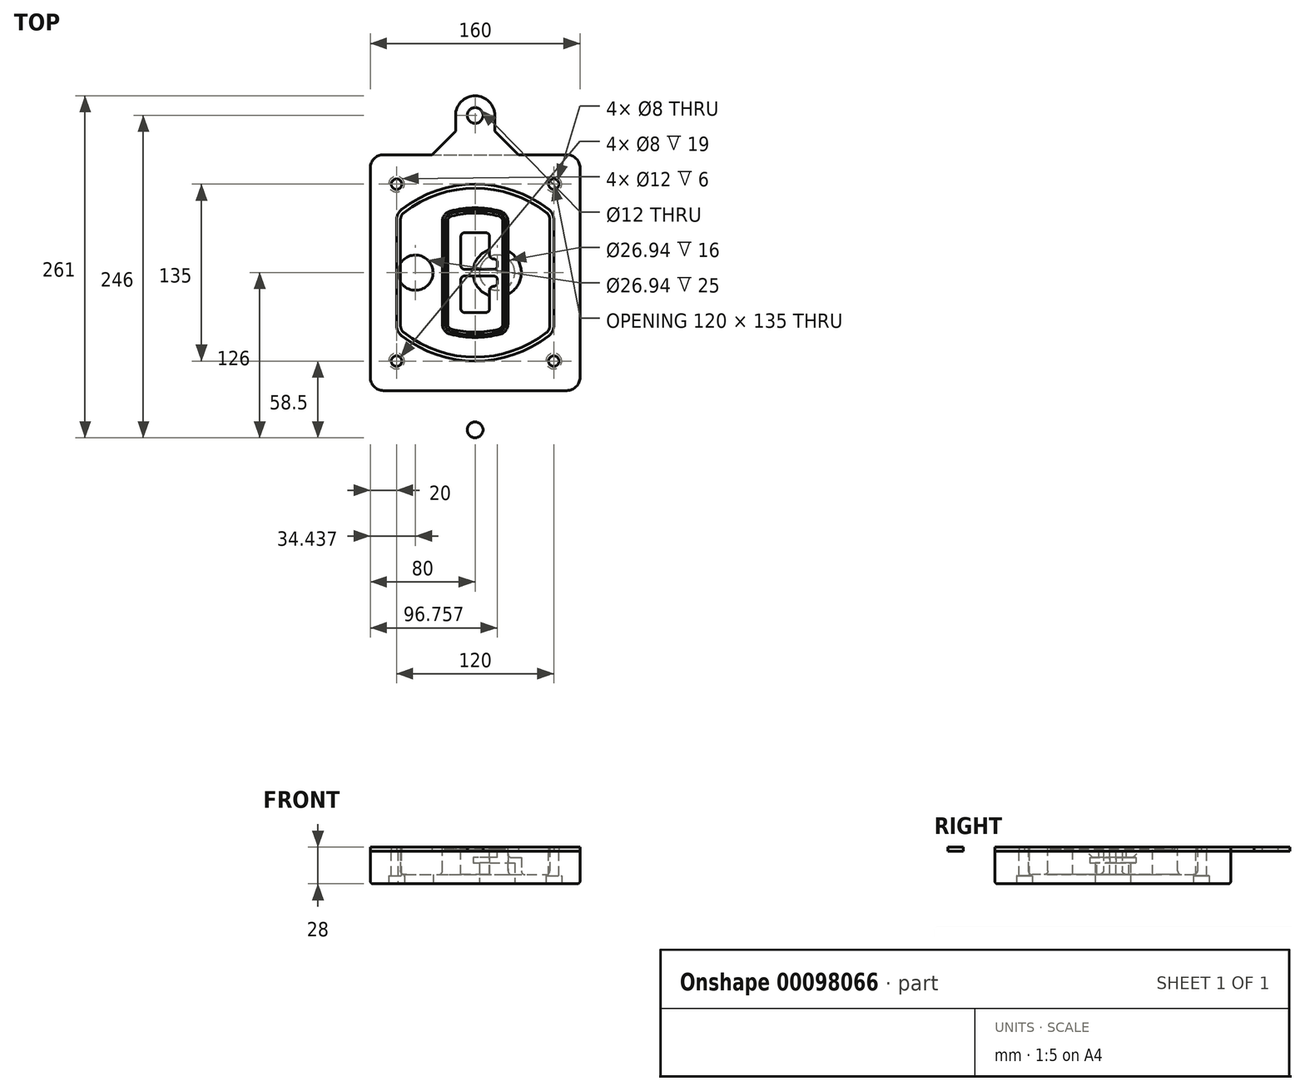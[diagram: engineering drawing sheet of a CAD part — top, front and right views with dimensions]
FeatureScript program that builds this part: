
annotation { "Feature Type Name" : "Feature", "Feature Type Description" : "" }
export const myFeature = defineFeature(function(context is Context, id is Id, definition is map)
    precondition{}
    {
        {
            var Q0;
            Q0=qCreatedBy(makeId("Top.planeOp"),FACE);
            var sketch = newSketch(context, id + "F0", { "sketchPlane" : qUnion([Q0])});
            skPoint(sketch, "E0.rect.middle", {"position": v(0, 0) * mm});
            skLineSegment(sketch, "E1.bottom", {"start": v(-70, -90) * mm, "end": v(70, -90) * mm});
            skLineSegment(sketch, "E1.top", {"start": v(-70, 90) * mm, "end": v(70, 90) * mm});
            skLineSegment(sketch, "E1.left", {"start": v(-80, -80) * mm, "end": v(-80, 80) * mm});
            skLineSegment(sketch, "E1.right", {"start": v(80, -80) * mm, "end": v(80, 80) * mm});
            skLineSegment(sketch, "E2", {"start": v(-80, 90) * mm, "end": v(80, -90) * mm, "construction": true});
            skLineSegment(sketch, "E3", {"start": v(80, 90) * mm, "end": v(-80, -90) * mm, "construction": true});
            skCircle(sketch, "E4", {"center": v(-60, 67.5) * mm, "radius": 4 * mm});
            skCircle(sketch, "E5", {"center": v(60, 67.5) * mm, "radius": 4 * mm});
            skCircle(sketch, "E6", {"center": v(60, -67.5) * mm, "radius": 4 * mm});
            skCircle(sketch, "E7", {"center": v(-60, -67.5) * mm, "radius": 4 * mm});
            skLineSegment(sketch, "E8", {"start": v(-60, 67.5) * mm, "end": v(60, 67.5) * mm, "construction": true});
            skLineSegment(sketch, "E9", {"start": v(60, 67.5) * mm, "end": v(60, -67.5) * mm, "construction": true});
            skLineSegment(sketch, "E10", {"start": v(60, -67.5) * mm, "end": v(-60, -67.5) * mm, "construction": true});
            skLineSegment(sketch, "E11", {"start": v(-60, -67.5) * mm, "end": v(-60, 67.5) * mm, "construction": true});
            skLineSegment(sketch, "E12", {"start": v(-60, 40.3) * mm, "end": v(-60, -40.3) * mm});
            skLineSegment(sketch, "E13", {"start": v(60, 40.3) * mm, "end": v(60, -40.3) * mm});
            skArc(sketch, "E14", {"start": v(56.15, 48.18) * mm, "mid": v(0, 67.5) * mm, "end": v(-56.15, 48.18) * mm});
            skArc(sketch, "E15", {"start": v(-56.15, -48.18) * mm, "mid": v(0, -67.5) * mm, "end": v(56.15, -48.18) * mm});
            skLineSegment(sketch, "E16", {"start": v(-60, 0) * mm, "end": v(60, 0) * mm, "construction": true});
            skPoint(sketch, "E17.visualSharp", {"position": v(-60, -45) * mm});
            skArc(sketch, "E17.filletArc", {"start": v(-60, -40.3) * mm, "mid": v(-58.99, -44.68) * mm, "end": v(-56.15, -48.18) * mm});
            skPoint(sketch, "E18.visualSharp", {"position": v(-60, 45) * mm});
            skArc(sketch, "E18.filletArc", {"start": v(-56.15, 48.18) * mm, "mid": v(-58.99, 44.68) * mm, "end": v(-60, 40.3) * mm});
            skPoint(sketch, "E19.visualSharp", {"position": v(60, 45) * mm});
            skArc(sketch, "E19.filletArc", {"start": v(60, 40.3) * mm, "mid": v(58.99, 44.68) * mm, "end": v(56.15, 48.18) * mm});
            skPoint(sketch, "E20.visualSharp", {"position": v(60, -45) * mm});
            skArc(sketch, "E20.filletArc", {"start": v(56.15, -48.18) * mm, "mid": v(58.99, -44.68) * mm, "end": v(60, -40.3) * mm});
            skPoint(sketch, "E21.visualSharp", {"position": v(-80, 90) * mm});
            skArc(sketch, "E21.filletArc", {"start": v(-70, 90) * mm, "mid": v(-77.07, 87.07) * mm, "end": v(-80, 80) * mm});
            skPoint(sketch, "E22.visualSharp", {"position": v(80, 90) * mm});
            skArc(sketch, "E22.filletArc", {"start": v(80, 80) * mm, "mid": v(77.07, 87.07) * mm, "end": v(70, 90) * mm});
            skPoint(sketch, "E23.visualSharp", {"position": v(80, -90) * mm});
            skArc(sketch, "E23.filletArc", {"start": v(70, -90) * mm, "mid": v(77.07, -87.07) * mm, "end": v(80, -80) * mm});
            skPoint(sketch, "E24.visualSharp", {"position": v(-80, -90) * mm});
            skArc(sketch, "E24.filletArc", {"start": v(-80, -80) * mm, "mid": v(-77.07, -87.07) * mm, "end": v(-70, -90) * mm});
            skArc(sketch, "E25.0", {"start": v(57, 40.3) * mm, "mid": v(56.3, 43.36) * mm, "end": v(54.3, 45.81) * mm});
            skLineSegment(sketch, "E25.1", {"start": v(57, 40.3) * mm, "end": v(57, -40.3) * mm});
            skArc(sketch, "E25.2", {"start": v(54.3, -45.81) * mm, "mid": v(56.3, -43.36) * mm, "end": v(57, -40.3) * mm});
            skArc(sketch, "E25.3", {"start": v(-54.3, -45.81) * mm, "mid": v(0, -64.5) * mm, "end": v(54.3, -45.81) * mm});
            skArc(sketch, "E25.4", {"start": v(-57, -40.3) * mm, "mid": v(-56.3, -43.36) * mm, "end": v(-54.3, -45.81) * mm});
            skArc(sketch, "E25.5", {"start": v(54.3, 45.81) * mm, "mid": v(0, 64.5) * mm, "end": v(-54.3, 45.81) * mm});
            skLineSegment(sketch, "E25.6", {"start": v(-57, 40.3) * mm, "end": v(-57, -40.3) * mm});
            skArc(sketch, "E25.7", {"start": v(-54.3, 45.81) * mm, "mid": v(-56.3, 43.36) * mm, "end": v(-57, 40.3) * mm});
            skArc(sketch, "E26.0", {"start": v(-58.62, 51.33) * mm, "mid": v(-62.58, 46.43) * mm, "end": v(-64, 40.3) * mm});
            skArc(sketch, "E26.1", {"start": v(58.62, 51.33) * mm, "mid": v(0, 71.5) * mm, "end": v(-58.62, 51.33) * mm});
            skArc(sketch, "E26.2", {"start": v(64, 40.3) * mm, "mid": v(62.58, 46.43) * mm, "end": v(58.62, 51.33) * mm});
            skLineSegment(sketch, "E26.3", {"start": v(64, 40.3) * mm, "end": v(64, -40.3) * mm});
            skArc(sketch, "E26.4", {"start": v(58.62, -51.33) * mm, "mid": v(62.58, -46.43) * mm, "end": v(64, -40.3) * mm});
            skLineSegment(sketch, "E26.5", {"start": v(-64, 40.3) * mm, "end": v(-64, -40.3) * mm});
            skArc(sketch, "E26.6", {"start": v(-58.62, -51.33) * mm, "mid": v(0, -71.5) * mm, "end": v(58.62, -51.33) * mm});
            skArc(sketch, "E26.7", {"start": v(-64, -40.3) * mm, "mid": v(-62.58, -46.43) * mm, "end": v(-58.62, -51.33) * mm});
            skSolve(sketch);
        }
        {
            var Q0;
            Q0=makeQuery(id+"F0.imprint","IMPRINT",FACE,{"disambiguationData":[TD([[makeQuery(id+"F0.imprint","IMPRINT",EDGE,{"derivedFrom":sQuery(id+"F0.wireOp",EDGE,"E1.bottom")}),1.0]])]});
            var Q1;
            Q1=makeQuery(id+"F0.imprint","IMPRINT",FACE,{"disambiguationData":[TD([[makeQuery(id+"F0.imprint","IMPRINT",EDGE,{"derivedFrom":sQuery(id+"F0.wireOp",EDGE,"E12")}),1.0]])]});
            var Q2;
            Q2=makeQuery(id+"F0.imprint","IMPRINT",FACE,{"disambiguationData":[TD([[makeQuery(id+"F0.imprint","IMPRINT",EDGE,{"derivedFrom":sQuery(id+"F0.wireOp",EDGE,"E25.0")}),1.0]])]});
            var Q3;
            Q3=makeQuery(id+"F0.imprint","IMPRINT",FACE,{"disambiguationData":[TD([[makeQuery(id+"F0.imprint","IMPRINT",EDGE,{"derivedFrom":sQuery(id+"F0.wireOp",EDGE,"E12")}),-1.0]])]});
            extrude(context, id + "F1", {"entities" : qUnion([Q0, Q1, Q2, Q3]), "oppositeDirection" : true, "depth" : 25 * mm});
        }
        {
            var Q0;
            Q0=makeQuery(id+"F0.imprint","IMPRINT",FACE,{"disambiguationData":[TD([[makeQuery(id+"F0.imprint","IMPRINT",EDGE,{"derivedFrom":sQuery(id+"F0.wireOp",EDGE,"E12")}),1.0]])]});
            extrude(context, id + "F2", {"entities" : qUnion([Q0]), "operationType" : NewBodyOperationType.ADD, "depth" : 3 * mm});
        }
        {
            var Q0;
            Q0=makeQuery(id+"F0.imprint","IMPRINT",FACE,{"disambiguationData":[TD([[makeQuery(id+"F0.imprint","IMPRINT",EDGE,{"derivedFrom":sQuery(id+"F0.wireOp",EDGE,"E25.0")}),1.0]])]});
            extrude(context, id + "F3", {"entities" : qUnion([Q0]), "operationType" : NewBodyOperationType.REMOVE, "oppositeDirection" : true, "depth" : 18 * mm});
        }
        {
            var Q0;
            Q0=makeQuery(id+"F2.opExtrude","CAP_FACE",FACE,{"disambiguationData":[OSD([sQuery(id+"F0.wireOp",EDGE,"E12"),sQuery(id+"F0.wireOp",EDGE,"E13"),sQuery(id+"F0.wireOp",EDGE,"E14"),sQuery(id+"F0.wireOp",EDGE,"E15"),sQuery(id+"F0.wireOp",EDGE,"E17.filletArc"),sQuery(id+"F0.wireOp",EDGE,"E18.filletArc"),sQuery(id+"F0.wireOp",EDGE,"E19.filletArc"),sQuery(id+"F0.wireOp",EDGE,"E20.filletArc"),sQuery(id+"F0.wireOp",EDGE,"E25.0"),sQuery(id+"F0.wireOp",EDGE,"E25.1"),sQuery(id+"F0.wireOp",EDGE,"E25.2"),sQuery(id+"F0.wireOp",EDGE,"E25.3"),sQuery(id+"F0.wireOp",EDGE,"E25.4"),sQuery(id+"F0.wireOp",EDGE,"E25.5"),sQuery(id+"F0.wireOp",EDGE,"E25.6"),sQuery(id+"F0.wireOp",EDGE,"E25.7")])],"isStart":false});
            var sketch = newSketch(context, id + "F4", { "sketchPlane" : qUnion([Q0])});
            skArc(sketch, "E27.0", {"start": v(-19.08, -46.97) * mm, "mid": v(0, -49.5) * mm, "end": v(19.08, -46.97) * mm});
            skArc(sketch, "E28.0", {"start": v(19.08, 46.97) * mm, "mid": v(0, 49.5) * mm, "end": v(-19.08, 46.97) * mm});
            skLineSegment(sketch, "E29", {"start": v(-25, 39.25) * mm, "end": v(-25, -39.25) * mm});
            skLineSegment(sketch, "E30", {"start": v(25, 39.25) * mm, "end": v(25, -39.25) * mm});
            skLineSegment(sketch, "E31", {"start": v(-25, 45.1) * mm, "end": v(25, 45.1) * mm, "construction": true});
            skLineSegment(sketch, "E32", {"start": v(-25, -45.1) * mm, "end": v(25, -45.1) * mm, "construction": true});
            skPoint(sketch, "E33.visualSharp", {"position": v(-25, 45.1) * mm});
            skArc(sketch, "E33.filletArc", {"start": v(-19.08, 46.97) * mm, "mid": v(-23.35, 44.11) * mm, "end": v(-25, 39.25) * mm});
            skPoint(sketch, "E34.visualSharp", {"position": v(25, 45.1) * mm});
            skArc(sketch, "E34.filletArc", {"start": v(25, 39.25) * mm, "mid": v(23.35, 44.11) * mm, "end": v(19.08, 46.97) * mm});
            skPoint(sketch, "E35.visualSharp", {"position": v(25, -45.1) * mm});
            skArc(sketch, "E35.filletArc", {"start": v(19.08, -46.97) * mm, "mid": v(23.35, -44.11) * mm, "end": v(25, -39.25) * mm});
            skPoint(sketch, "E36.visualSharp", {"position": v(-25, -45.1) * mm});
            skArc(sketch, "E36.filletArc", {"start": v(-25, -39.25) * mm, "mid": v(-23.35, -44.11) * mm, "end": v(-19.08, -46.97) * mm});
            skArc(sketch, "E37.0", {"start": v(54.3, 45.81) * mm, "mid": v(0, 64.5) * mm, "end": v(-54.3, 45.81) * mm});
            skArc(sketch, "E37.1", {"start": v(-54.3, 45.81) * mm, "mid": v(-56.3, 43.36) * mm, "end": v(-57, 40.3) * mm});
            skLineSegment(sketch, "E37.2", {"start": v(-57, 40.3) * mm, "end": v(-57, -40.3) * mm});
            skArc(sketch, "E37.3", {"start": v(-57, -40.3) * mm, "mid": v(-56.3, -43.36) * mm, "end": v(-54.3, -45.81) * mm});
            skArc(sketch, "E37.4", {"start": v(-54.3, -45.81) * mm, "mid": v(0, -64.5) * mm, "end": v(54.3, -45.81) * mm});
            skArc(sketch, "E37.5", {"start": v(54.3, -45.81) * mm, "mid": v(56.3, -43.36) * mm, "end": v(57, -40.3) * mm});
            skLineSegment(sketch, "E37.6", {"start": v(57, 40.3) * mm, "end": v(57, -40.3) * mm});
            skArc(sketch, "E37.7", {"start": v(57, 40.3) * mm, "mid": v(56.3, 43.36) * mm, "end": v(54.3, 45.81) * mm});
            skLineSegment(sketch, "E38.0", {"start": v(23, 39.25) * mm, "end": v(23, -39.25) * mm});
            skArc(sketch, "E38.1", {"start": v(18.56, -45.04) * mm, "mid": v(21.76, -42.9) * mm, "end": v(23, -39.25) * mm});
            skArc(sketch, "E38.2", {"start": v(-18.56, -45.04) * mm, "mid": v(0, -47.5) * mm, "end": v(18.56, -45.04) * mm});
            skArc(sketch, "E38.3", {"start": v(-23, -39.25) * mm, "mid": v(-21.76, -42.9) * mm, "end": v(-18.56, -45.04) * mm});
            skLineSegment(sketch, "E38.4", {"start": v(-23, 39.25) * mm, "end": v(-23, -39.25) * mm});
            skArc(sketch, "E38.5", {"start": v(23, 39.25) * mm, "mid": v(21.76, 42.9) * mm, "end": v(18.56, 45.04) * mm});
            skArc(sketch, "E38.6", {"start": v(-18.56, 45.04) * mm, "mid": v(-21.76, 42.9) * mm, "end": v(-23, 39.25) * mm});
            skArc(sketch, "E38.7", {"start": v(18.56, 45.04) * mm, "mid": v(0, 47.5) * mm, "end": v(-18.56, 45.04) * mm});
            skArc(sketch, "E39.0", {"start": v(21, 39.25) * mm, "mid": v(20.18, 41.68) * mm, "end": v(18.04, 43.1) * mm});
            skLineSegment(sketch, "E39.1", {"start": v(21, 39.25) * mm, "end": v(21, -39.25) * mm});
            skArc(sketch, "E39.2", {"start": v(18.04, -43.1) * mm, "mid": v(20.18, -41.68) * mm, "end": v(21, -39.25) * mm});
            skArc(sketch, "E39.3", {"start": v(-18.04, -43.1) * mm, "mid": v(0, -45.5) * mm, "end": v(18.04, -43.1) * mm});
            skArc(sketch, "E39.4", {"start": v(-21, -39.25) * mm, "mid": v(-20.18, -41.68) * mm, "end": v(-18.04, -43.1) * mm});
            skArc(sketch, "E39.5", {"start": v(18.04, 43.1) * mm, "mid": v(0, 45.5) * mm, "end": v(-18.04, 43.1) * mm});
            skLineSegment(sketch, "E39.6", {"start": v(-21, 39.25) * mm, "end": v(-21, -39.25) * mm});
            skArc(sketch, "E39.7", {"start": v(-18.04, 43.1) * mm, "mid": v(-20.18, 41.68) * mm, "end": v(-21, 39.25) * mm});
            skLineSegment(sketch, "E40", {"start": v(-25, 0) * mm, "end": v(25, 0) * mm, "construction": true});
            skLineSegment(sketch, "E41", {"start": v(-11, 5.5) * mm, "end": v(-11, 27.5) * mm});
            skLineSegment(sketch, "E42", {"start": v(-8, 30.5) * mm, "end": v(8, 30.5) * mm});
            skLineSegment(sketch, "E43", {"start": v(11, 27.5) * mm, "end": v(11, 13.5) * mm});
            skLineSegment(sketch, "E44", {"start": v(14, 10.5) * mm, "end": v(14, 10.5) * mm});
            skLineSegment(sketch, "E45", {"start": v(17, 7.5) * mm, "end": v(17, 5.5) * mm});
            skLineSegment(sketch, "E46", {"start": v(14, 2.5) * mm, "end": v(-8, 2.5) * mm});
            skPoint(sketch, "E47.visualSharp", {"position": v(-11, 30.5) * mm});
            skArc(sketch, "E47.filletArc", {"start": v(-8, 30.5) * mm, "mid": v(-10.12, 29.62) * mm, "end": v(-11, 27.5) * mm});
            skPoint(sketch, "E48.visualSharp", {"position": v(11, 30.5) * mm});
            skArc(sketch, "E48.filletArc", {"start": v(11, 27.5) * mm, "mid": v(10.12, 29.62) * mm, "end": v(8, 30.5) * mm});
            skPoint(sketch, "E49.visualSharp", {"position": v(11, 10.5) * mm});
            skArc(sketch, "E49.filletArc", {"start": v(11, 13.5) * mm, "mid": v(11.88, 11.38) * mm, "end": v(14, 10.5) * mm});
            skPoint(sketch, "E50.visualSharp", {"position": v(17, 10.5) * mm});
            skArc(sketch, "E50.filletArc", {"start": v(17, 7.5) * mm, "mid": v(16.12, 9.62) * mm, "end": v(14, 10.5) * mm});
            skPoint(sketch, "E51.visualSharp", {"position": v(17, 2.5) * mm});
            skArc(sketch, "E51.filletArc", {"start": v(14, 2.5) * mm, "mid": v(16.12, 3.38) * mm, "end": v(17, 5.5) * mm});
            skPoint(sketch, "E52.visualSharp", {"position": v(-11, 2.5) * mm});
            skArc(sketch, "E52.filletArc", {"start": v(-11, 5.5) * mm, "mid": v(-10.12, 3.38) * mm, "end": v(-8, 2.5) * mm});
            skLineSegment(sketch, "E53.0.MirrorCS", {"start": v(14, -2.5) * mm, "end": v(-8, -2.5) * mm});
            skArc(sketch, "E54.0.MirrorCS", {"start": v(-11, -5.5) * mm, "mid": v(-10.12, -3.38) * mm, "end": v(-8, -2.5) * mm});
            skLineSegment(sketch, "E55.0.MirrorCS", {"start": v(-11, -5.5) * mm, "end": v(-11, -27.5) * mm});
            skArc(sketch, "E56.0.MirrorCS", {"start": v(-8, -30.5) * mm, "mid": v(-10.12, -29.62) * mm, "end": v(-11, -27.5) * mm});
            skLineSegment(sketch, "E57.0.MirrorCS", {"start": v(-8, -30.5) * mm, "end": v(8, -30.5) * mm});
            skArc(sketch, "E58.0.MirrorCS", {"start": v(11, -27.5) * mm, "mid": v(10.12, -29.62) * mm, "end": v(8, -30.5) * mm});
            skLineSegment(sketch, "E59.0.MirrorCS", {"start": v(11, -27.5) * mm, "end": v(11, -13.5) * mm});
            skArc(sketch, "E60.0.MirrorCS", {"start": v(11, -13.5) * mm, "mid": v(11.88, -11.38) * mm, "end": v(14, -10.5) * mm});
            skArc(sketch, "E61.0.MirrorCS", {"start": v(17, -7.5) * mm, "mid": v(16.12, -9.62) * mm, "end": v(14, -10.5) * mm});
            skLineSegment(sketch, "E62.0.MirrorCS", {"start": v(17, -7.5) * mm, "end": v(17, -5.5) * mm});
            skArc(sketch, "E63.0.MirrorCS", {"start": v(14, -2.5) * mm, "mid": v(16.12, -3.38) * mm, "end": v(17, -5.5) * mm});
            skSolve(sketch);
        }
        {
            var Q0;
            Q0=makeQuery(id+"F4.imprint","IMPRINT",FACE,{"disambiguationData":[TD([[makeQuery(id+"F4.imprint","IMPRINT",EDGE,{"derivedFrom":sQuery(id+"F4.wireOp",EDGE,"E27.0")}),1.0]])]});
            var Q1;
            Q1=makeQuery(id+"F4.imprint","IMPRINT",FACE,{"disambiguationData":[TD([[makeQuery(id+"F4.imprint","IMPRINT",EDGE,{"derivedFrom":sQuery(id+"F4.wireOp",EDGE,"E38.0")}),-1.0]])]});
            var Q2;
            Q2=makeQuery(id+"F4.imprint","IMPRINT",FACE,{"disambiguationData":[TD([[makeQuery(id+"F4.imprint","IMPRINT",EDGE,{"derivedFrom":sQuery(id+"F4.wireOp",EDGE,"E39.0")}),1.0]])]});
            extrude(context, id + "F5", {"entities" : qUnion([Q0, Q1, Q2]), "operationType" : NewBodyOperationType.ADD, "endBound" : BoundingType.UP_TO_NEXT, "oppositeDirection" : true, "depth" : 25 * mm});
        }
        {
            var Q0;
            Q0=makeQuery(id+"F4.imprint","IMPRINT",FACE,{"disambiguationData":[TD([[makeQuery(id+"F4.imprint","IMPRINT",EDGE,{"derivedFrom":sQuery(id+"F4.wireOp",EDGE,"E38.0")}),-1.0]])]});
            extrude(context, id + "F6", {"entities" : qUnion([Q0]), "operationType" : NewBodyOperationType.REMOVE, "oppositeDirection" : true, "depth" : 2 * mm});
        }
        {
            var Q0;
            Q0=makeQuery(id+"F1.opExtrude","CAP_FACE",FACE,{"disambiguationData":[OSD([sQuery(id+"F0.wireOp",EDGE,"E1.bottom"),sQuery(id+"F0.wireOp",EDGE,"E1.top"),sQuery(id+"F0.wireOp",EDGE,"E1.left"),sQuery(id+"F0.wireOp",EDGE,"E1.right"),sQuery(id+"F0.wireOp",EDGE,"E4"),sQuery(id+"F0.wireOp",EDGE,"E5"),sQuery(id+"F0.wireOp",EDGE,"E6"),sQuery(id+"F0.wireOp",EDGE,"E7"),sQuery(id+"F0.wireOp",EDGE,"E21.filletArc"),sQuery(id+"F0.wireOp",EDGE,"E22.filletArc"),sQuery(id+"F0.wireOp",EDGE,"E23.filletArc"),sQuery(id+"F0.wireOp",EDGE,"E24.filletArc")])],"isStart":false});
            var sketch = newSketch(context, id + "F7", { "sketchPlane" : qUnion([Q0])});
            skCircle(sketch, "E64", {"center": v(16.76, 0) * mm, "radius": 13.47 * mm});
            skCircle(sketch, "E65", {"center": v(-45.56, 0) * mm, "radius": 13.47 * mm});
            skLineSegment(sketch, "E66", {"start": v(80, 0) * mm, "end": v(-80, 0) * mm});
            skCircle(sketch, "E67", {"center": v(16.76, 0) * mm, "radius": 18.47 * mm});
            skCircle(sketch, "E68", {"center": v(60, -67.5) * mm, "radius": 6 * mm});
            skCircle(sketch, "E69", {"center": v(-60, -67.5) * mm, "radius": 6 * mm});
            skCircle(sketch, "E70", {"center": v(-60, 67.5) * mm, "radius": 6 * mm});
            skCircle(sketch, "E71", {"center": v(60, 67.5) * mm, "radius": 6 * mm});
            skSolve(sketch);
        }
        {
            var Q0;
            {var subQ1=sQuery(id+"F7.wireOp",EDGE,"E66");var subQ4=sQuery(id+"F7.wireOp",EDGE,"E64");var subQ6=makeQuery(id+"F7.imprint","INTERSECT",VERTEX,{"disambiguationData":[OD(0.0)],"derivedFrom":[subQ4,subQ1]});Q0=makeQuery(id+"F7.imprint","IMPRINT",FACE,{"disambiguationData":[TD([[makeQuery(id+"F7.imprint","IMPRINT",EDGE,{"disambiguationData":[TD([[subQ6,-1.0]])],"derivedFrom":subQ4}),-1.0]])]});}
            var Q1;
            {var subQ0=sQuery(id+"F7.wireOp",EDGE,"E66");var subQ1=sQuery(id+"F7.wireOp",EDGE,"E64");var subQ3=makeQuery(id+"F7.imprint","INTERSECT",VERTEX,{"disambiguationData":[OD(0.0)],"derivedFrom":[subQ1,subQ0]});Q1=makeQuery(id+"F7.imprint","IMPRINT",FACE,{"disambiguationData":[TD([[makeQuery(id+"F7.imprint","IMPRINT",EDGE,{"disambiguationData":[TD([[subQ3,-1.0]])],"derivedFrom":subQ1}),1.0]])]});}
            var Q2;
            {var subQ0=sQuery(id+"F7.wireOp",EDGE,"E66");var subQ1=sQuery(id+"F7.wireOp",EDGE,"E64");var subQ3=makeQuery(id+"F7.imprint","INTERSECT",VERTEX,{"disambiguationData":[OD(0.0)],"derivedFrom":[subQ1,subQ0]});Q2=makeQuery(id+"F7.imprint","IMPRINT",FACE,{"disambiguationData":[TD([[makeQuery(id+"F7.imprint","IMPRINT",EDGE,{"disambiguationData":[TD([[subQ3,1.0]])],"derivedFrom":subQ1}),1.0]])]});}
            var Q3;
            {var subQ1=sQuery(id+"F7.wireOp",EDGE,"E66");var subQ4=sQuery(id+"F7.wireOp",EDGE,"E64");var subQ6=makeQuery(id+"F7.imprint","INTERSECT",VERTEX,{"disambiguationData":[OD(0.0)],"derivedFrom":[subQ4,subQ1]});Q3=makeQuery(id+"F7.imprint","IMPRINT",FACE,{"disambiguationData":[TD([[makeQuery(id+"F7.imprint","IMPRINT",EDGE,{"disambiguationData":[TD([[subQ6,1.0]])],"derivedFrom":subQ4}),-1.0]])]});}
            extrude(context, id + "F8", {"entities" : qUnion([Q0, Q1, Q2, Q3]), "operationType" : NewBodyOperationType.ADD, "oppositeDirection" : true, "depth" : 20 * mm});
        }
        {
            var Q0;
            {var subQ0=sQuery(id+"F7.wireOp",EDGE,"E66");var subQ1=sQuery(id+"F7.wireOp",EDGE,"E64");var subQ3=makeQuery(id+"F7.imprint","INTERSECT",VERTEX,{"disambiguationData":[OD(0.0)],"derivedFrom":[subQ1,subQ0]});Q0=makeQuery(id+"F7.imprint","IMPRINT",FACE,{"disambiguationData":[TD([[makeQuery(id+"F7.imprint","IMPRINT",EDGE,{"disambiguationData":[TD([[subQ3,-1.0]])],"derivedFrom":subQ1}),1.0]])]});}
            var Q1;
            {var subQ0=sQuery(id+"F7.wireOp",EDGE,"E66");var subQ1=sQuery(id+"F7.wireOp",EDGE,"E64");var subQ3=makeQuery(id+"F7.imprint","INTERSECT",VERTEX,{"disambiguationData":[OD(0.0)],"derivedFrom":[subQ1,subQ0]});Q1=makeQuery(id+"F7.imprint","IMPRINT",FACE,{"disambiguationData":[TD([[makeQuery(id+"F7.imprint","IMPRINT",EDGE,{"disambiguationData":[TD([[subQ3,1.0]])],"derivedFrom":subQ1}),1.0]])]});}
            extrude(context, id + "F9", {"entities" : qUnion([Q0, Q1]), "operationType" : NewBodyOperationType.REMOVE, "oppositeDirection" : true, "depth" : 16 * mm});
        }
        {
            var Q0;
            {var subQ0=sQuery(id+"F7.wireOp",EDGE,"E66");var subQ1=sQuery(id+"F7.wireOp",EDGE,"E65");var subQ3=makeQuery(id+"F7.imprint","INTERSECT",VERTEX,{"disambiguationData":[OD(0.0)],"derivedFrom":[subQ1,subQ0]});Q0=makeQuery(id+"F7.imprint","IMPRINT",FACE,{"disambiguationData":[TD([[makeQuery(id+"F7.imprint","IMPRINT",EDGE,{"disambiguationData":[TD([[subQ3,-1.0]])],"derivedFrom":subQ1}),1.0]])]});}
            var Q1;
            {var subQ0=sQuery(id+"F7.wireOp",EDGE,"E66");var subQ1=sQuery(id+"F7.wireOp",EDGE,"E65");var subQ3=makeQuery(id+"F7.imprint","INTERSECT",VERTEX,{"disambiguationData":[OD(0.0)],"derivedFrom":[subQ1,subQ0]});Q1=makeQuery(id+"F7.imprint","IMPRINT",FACE,{"disambiguationData":[TD([[makeQuery(id+"F7.imprint","IMPRINT",EDGE,{"disambiguationData":[TD([[subQ3,1.0]])],"derivedFrom":subQ1}),1.0]])]});}
            extrude(context, id + "F10", {"entities" : qUnion([Q0, Q1]), "operationType" : NewBodyOperationType.REMOVE, "oppositeDirection" : true, "depth" : 25 * mm});
        }
        {
            var Q0;
            Q0=makeQuery(id+"F7.imprint","IMPRINT",FACE,{"disambiguationData":[TD([[makeQuery(id+"F7.imprint","IMPRINT",EDGE,{"derivedFrom":sQuery(id+"F7.wireOp",EDGE,"E68")}),1.0]])]});
            var Q1;
            Q1=makeQuery(id+"F7.imprint","IMPRINT",FACE,{"disambiguationData":[TD([[makeQuery(id+"F7.imprint","IMPRINT",EDGE,{"derivedFrom":makeQuery(id+"F1.opExtrude","CAP_EDGE",EDGE,{"disambiguationData":[OSD([sQuery(id+"F0.wireOp",EDGE,"E5")])],"isStart":false})}),-1.0]])]});
            var Q2;
            Q2=makeQuery(id+"F7.imprint","IMPRINT",FACE,{"disambiguationData":[TD([[makeQuery(id+"F7.imprint","IMPRINT",EDGE,{"derivedFrom":sQuery(id+"F7.wireOp",EDGE,"E69")}),1.0]])]});
            var Q3;
            Q3=makeQuery(id+"F7.imprint","IMPRINT",FACE,{"disambiguationData":[TD([[makeQuery(id+"F7.imprint","IMPRINT",EDGE,{"derivedFrom":makeQuery(id+"F1.opExtrude","CAP_EDGE",EDGE,{"disambiguationData":[OSD([sQuery(id+"F0.wireOp",EDGE,"E4")])],"isStart":false})}),-1.0]])]});
            var Q4;
            Q4=makeQuery(id+"F7.imprint","IMPRINT",FACE,{"disambiguationData":[TD([[makeQuery(id+"F7.imprint","IMPRINT",EDGE,{"derivedFrom":sQuery(id+"F7.wireOp",EDGE,"E70")}),1.0]])]});
            var Q5;
            Q5=makeQuery(id+"F7.imprint","IMPRINT",FACE,{"disambiguationData":[TD([[makeQuery(id+"F7.imprint","IMPRINT",EDGE,{"derivedFrom":makeQuery(id+"F1.opExtrude","CAP_EDGE",EDGE,{"disambiguationData":[OSD([sQuery(id+"F0.wireOp",EDGE,"E7")])],"isStart":false})}),-1.0]])]});
            var Q6;
            Q6=makeQuery(id+"F7.imprint","IMPRINT",FACE,{"disambiguationData":[TD([[makeQuery(id+"F7.imprint","IMPRINT",EDGE,{"derivedFrom":sQuery(id+"F7.wireOp",EDGE,"E71")}),1.0]])]});
            var Q7;
            Q7=makeQuery(id+"F7.imprint","IMPRINT",FACE,{"disambiguationData":[TD([[makeQuery(id+"F7.imprint","IMPRINT",EDGE,{"derivedFrom":makeQuery(id+"F1.opExtrude","CAP_EDGE",EDGE,{"disambiguationData":[OSD([sQuery(id+"F0.wireOp",EDGE,"E6")])],"isStart":false})}),-1.0]])]});
            extrude(context, id + "F11", {"entities" : qUnion([Q0, Q1, Q2, Q3, Q4, Q5, Q6, Q7]), "operationType" : NewBodyOperationType.REMOVE, "oppositeDirection" : true, "depth" : 6 * mm});
        }
        {
            var Q0;
            Q0=makeQuery(id+"F9.boolean.opBoolean","COPY",FACE,{"derivedFrom":makeQuery(id+"F9.opExtrude","CAP_FACE",FACE,{"disambiguationData":[OSD([sQuery(id+"F7.wireOp",EDGE,"E64")])],"isStart":false})});
            var sketch = newSketch(context, id + "F12", { "sketchPlane" : qUnion([Q0])});
            skArc(sketch, "E72.0", {"start": v(11, 17.55) * mm, "mid": v(2.57, 11.82) * mm, "end": v(-1.54, 2.5) * mm});
            skArc(sketch, "E72.1", {"start": v(-1.54, -2.5) * mm, "mid": v(2.57, -11.82) * mm, "end": v(11, -17.55) * mm});
            skLineSegment(sketch, "E73", {"start": v(-1.54, -2.5) * mm, "end": v(14, -2.5) * mm});
            skLineSegment(sketch, "E74.0", {"start": v(14, 2.5) * mm, "end": v(-1.54, 2.5) * mm});
            skArc(sketch, "E74.1", {"start": v(14, 2.5) * mm, "mid": v(16.12, 3.38) * mm, "end": v(17, 5.5) * mm});
            skLineSegment(sketch, "E74.2", {"start": v(17, 7.5) * mm, "end": v(17, 5.5) * mm});
            skArc(sketch, "E74.3", {"start": v(17, 7.5) * mm, "mid": v(16.12, 9.62) * mm, "end": v(14, 10.5) * mm});
            skArc(sketch, "E74.4", {"start": v(11, 13.5) * mm, "mid": v(11.88, 11.38) * mm, "end": v(14, 10.5) * mm});
            skLineSegment(sketch, "E74.5", {"start": v(11, 17.55) * mm, "end": v(11, 13.5) * mm});
            skLineSegment(sketch, "E74.7", {"start": v(14, -2.5) * mm, "end": v(-1.54, -2.5) * mm});
            skArc(sketch, "E74.8", {"start": v(14, -2.5) * mm, "mid": v(16.12, -3.38) * mm, "end": v(17, -5.5) * mm});
            skLineSegment(sketch, "E74.9", {"start": v(17, -7.5) * mm, "end": v(17, -5.5) * mm});
            skArc(sketch, "E74.10", {"start": v(17, -7.5) * mm, "mid": v(16.12, -9.62) * mm, "end": v(14, -10.5) * mm});
            skArc(sketch, "E74.11", {"start": v(11, -13.5) * mm, "mid": v(11.88, -11.38) * mm, "end": v(14, -10.5) * mm});
            skLineSegment(sketch, "E74.12", {"start": v(11, -17.55) * mm, "end": v(11, -13.5) * mm});
            skPoint(sketch, "E75.orphan", {"position": v(11, -27.5) * mm});
            skPoint(sketch, "E76.orphan", {"position": v(-8, -2.5) * mm});
            skPoint(sketch, "E77.orphan", {"position": v(-8, 2.5) * mm});
            skPoint(sketch, "E78.orphan", {"position": v(11, 27.5) * mm});
            skSolve(sketch);
        }
        {
            var Q0;
            {var subQ7=sQuery(id+"F12.wireOp",EDGE,"E72.0");var subQ14=sQuery(id+"F12.wireOp",EDGE,"E72.1");var subQ16=sQuery(id+"F12.wireOp",EDGE,"E74.1");var subQ18=sQuery(id+"F12.wireOp",EDGE,"E74.8");Q0=qUnion([makeQuery(id+"F12.imprint","IMPRINT",FACE,{"disambiguationData":[TD([[makeQuery(id+"F12.imprint","IMPRINT",EDGE,{"derivedFrom":subQ7}),1.0]])]}),makeQuery(id+"F12.imprint","IMPRINT",FACE,{"disambiguationData":[TD([[makeQuery(id+"F12.imprint","IMPRINT",EDGE,{"derivedFrom":subQ14}),1.0]])]}),makeQuery(id+"F12.imprint","IMPRINT",FACE,{"disambiguationData":[TD([[makeQuery(id+"F12.imprint","IMPRINT",EDGE,{"derivedFrom":subQ16}),1.0]])]}),makeQuery(id+"F12.imprint","IMPRINT",FACE,{"disambiguationData":[TD([[makeQuery(id+"F12.imprint","IMPRINT",EDGE,{"derivedFrom":subQ18}),-1.0]])]})]);}
            var Q1;
            Q1=makeQuery(id+"F5.boolean.opBoolean","SPLIT",FACE,{"disambiguationData":[TD([makeQuery(id+"F5.opExtrude","SWEPT_FACE",FACE,{"disambiguationData":[OSD([sQuery(id+"F4.wireOp",EDGE,"E41")])]})])],"derivedFrom":makeQuery(id+"F3.boolean.opBoolean","COPY",FACE,{"derivedFrom":makeQuery(id+"F3.opExtrude","CAP_FACE",FACE,{"disambiguationData":[OSD([sQuery(id+"F0.wireOp",EDGE,"E25.0"),sQuery(id+"F0.wireOp",EDGE,"E25.1"),sQuery(id+"F0.wireOp",EDGE,"E25.2"),sQuery(id+"F0.wireOp",EDGE,"E25.3"),sQuery(id+"F0.wireOp",EDGE,"E25.4"),sQuery(id+"F0.wireOp",EDGE,"E25.5"),sQuery(id+"F0.wireOp",EDGE,"E25.6"),sQuery(id+"F0.wireOp",EDGE,"E25.7")])],"isStart":false})})});
            extrude(context, id + "F13", {"entities" : qUnion([Q0]), "operationType" : NewBodyOperationType.REMOVE, "endBound" : BoundingType.UP_TO_SURFACE, "endBoundEntityFace" : qUnion([Q1]), "depth" : 25 * mm});
        }
        {
            var Q0;
            Q0=makeQuery(id+"F3.boolean.opBoolean","COPY",EDGE,{"derivedFrom":makeQuery(id+"F3.opExtrude","CAP_EDGE",EDGE,{"disambiguationData":[OSD([sQuery(id+"F0.wireOp",EDGE,"E25.6")])],"isStart":false})});
            var Q1;
            Q1=makeQuery(id+"F8.boolean.opBoolean","INTERSECT",EDGE,{"derivedFrom":[makeQuery(id+"F5.opExtrude","SWEPT_FACE",FACE,{"disambiguationData":[OSD([sQuery(id+"F4.wireOp",EDGE,"E30")])]}),makeQuery(id+"F8.opExtrude","CAP_FACE",FACE,{"disambiguationData":[OSD([sQuery(id+"F7.wireOp",EDGE,"E67")])],"isStart":false})]});
            var Q2;
            Q2=makeQuery(id+"F8.boolean.opBoolean","INTERSECT",EDGE,{"disambiguationData":[OD(1.0)],"derivedFrom":[makeQuery(id+"F5.opExtrude","SWEPT_FACE",FACE,{"disambiguationData":[OSD([sQuery(id+"F4.wireOp",EDGE,"E30")])]}),makeQuery(id+"F8.opExtrude","SWEPT_FACE",FACE,{"disambiguationData":[OSD([sQuery(id+"F7.wireOp",EDGE,"E67")])]})]});
            var Q3;
            {var subQ0=sQuery(id+"F4.wireOp",EDGE,"E30");Q3=makeQuery(id+"F8.boolean.opBoolean","SPLIT",EDGE,{"disambiguationData":[TD([makeQuery(id+"F5.opExtrude","SWEPT_FACE",FACE,{"disambiguationData":[OSD([sQuery(id+"F4.wireOp",EDGE,"E35.filletArc")])]})])],"derivedFrom":makeQuery(id+"F5.opExtrude","CAP_EDGE",EDGE,{"disambiguationData":[OSD([subQ0])],"isStart":false})});}
            var Q4;
            {var subQ0=sQuery(id+"F0.wireOp",EDGE,"E25.7");var subQ1=sQuery(id+"F0.wireOp",EDGE,"E25.1");var subQ2=sQuery(id+"F0.wireOp",EDGE,"E25.6");var subQ3=sQuery(id+"F0.wireOp",EDGE,"E25.5");var subQ4=sQuery(id+"F0.wireOp",EDGE,"E25.4");var subQ5=sQuery(id+"F0.wireOp",EDGE,"E25.0");var subQ6=sQuery(id+"F0.wireOp",EDGE,"E25.2");var subQ7=sQuery(id+"F0.wireOp",EDGE,"E25.3");Q4=makeQuery(id+"F8.boolean.opBoolean","INTERSECT",EDGE,{"derivedFrom":[makeQuery(id+"F5.boolean.opBoolean","SPLIT",FACE,{"disambiguationData":[TD([makeQuery(id+"F2.opExtrude","SWEPT_FACE",FACE,{"disambiguationData":[OSD([subQ5])]})])],"derivedFrom":makeQuery(id+"F3.boolean.opBoolean","COPY",FACE,{"derivedFrom":makeQuery(id+"F3.opExtrude","CAP_FACE",FACE,{"disambiguationData":[OSD([subQ5,subQ1,subQ6,subQ7,subQ4,subQ3,subQ2,subQ0])],"isStart":false})})}),makeQuery(id+"F8.opExtrude","SWEPT_FACE",FACE,{"disambiguationData":[OSD([sQuery(id+"F7.wireOp",EDGE,"E67")])]})]});}
            var Q5;
            Q5=makeQuery(id+"F8.boolean.opBoolean","INTERSECT",EDGE,{"disambiguationData":[OD(0.0)],"derivedFrom":[makeQuery(id+"F5.opExtrude","SWEPT_FACE",FACE,{"disambiguationData":[OSD([sQuery(id+"F4.wireOp",EDGE,"E30")])]}),makeQuery(id+"F8.opExtrude","SWEPT_FACE",FACE,{"disambiguationData":[OSD([sQuery(id+"F7.wireOp",EDGE,"E67")])]})]});
            fillet(context, id + "F14", {"entities" : qUnion([Q0, Q1, Q2, Q3, Q4, Q5]), "radius" : 3 * mm, "tangentPropagation" : true, "allowEdgeOverflow" : false});
        }
        {
            var Q0;
            Q0=makeQuery(id+"F1.opExtrude","CAP_EDGE",EDGE,{"disambiguationData":[OSD([sQuery(id+"F0.wireOp",EDGE,"E1.bottom")])],"isStart":false});
            fillet(context, id + "F15", {"entities" : qUnion([Q0]), "radius" : 2 * mm, "tangentPropagation" : true, "allowEdgeOverflow" : false});
        }
        {
            var Q0;
            {var subQ0=sQuery(id+"F0.wireOp",EDGE,"E22.filletArc");var subQ1=sQuery(id+"F0.wireOp",EDGE,"E7");var subQ2=sQuery(id+"F0.wireOp",EDGE,"E6");var subQ3=sQuery(id+"F0.wireOp",EDGE,"E5");var subQ4=sQuery(id+"F0.wireOp",EDGE,"E4");var subQ5=sQuery(id+"F0.wireOp",EDGE,"E1.bottom");var subQ6=sQuery(id+"F0.wireOp",EDGE,"E21.filletArc");var subQ7=sQuery(id+"F0.wireOp",EDGE,"E1.top");var subQ8=sQuery(id+"F0.wireOp",EDGE,"E1.left");var subQ9=sQuery(id+"F0.wireOp",EDGE,"E1.right");var subQ10=sQuery(id+"F0.wireOp",EDGE,"E23.filletArc");var subQ11=sQuery(id+"F0.wireOp",EDGE,"E24.filletArc");Q0=makeQuery(id+"F2.boolean.opBoolean","SPLIT",FACE,{"disambiguationData":[TD([makeQuery(id+"F1.opExtrude","SWEPT_FACE",FACE,{"disambiguationData":[OSD([subQ5])]})])],"derivedFrom":makeQuery(id+"F1.opExtrude","CAP_FACE",FACE,{"disambiguationData":[OSD([subQ5,subQ7,subQ8,subQ9,subQ4,subQ3,subQ2,subQ1,subQ6,subQ0,subQ10,subQ11])],"isStart":true})});}
            var sketch = newSketch(context, id + "F16", { "sketchPlane" : qUnion([Q0])});
            skPoint(sketch, "E79", {"position": v(-60, 67.5) * mm});
            skPoint(sketch, "E80", {"position": v(-60, -67.5) * mm});
            skPoint(sketch, "E81", {"position": v(60, -67.5) * mm});
            skPoint(sketch, "E82", {"position": v(60, 67.5) * mm});
            skPoint(sketch, "E83", {"position": v(70, 80) * mm});
            skPoint(sketch, "E84", {"position": v(-70, 80) * mm});
            skPoint(sketch, "E85", {"position": v(0, 80) * mm});
            skPoint(sketch, "E86", {"position": v(-70, -80) * mm});
            skPoint(sketch, "E87", {"position": v(70, -80) * mm});
            skPoint(sketch, "E88", {"position": v(0, -80) * mm});
            skPoint(sketch, "E89", {"position": v(50, 40.3) * mm});
            skPoint(sketch, "E90", {"position": v(50, -40.3) * mm});
            skPoint(sketch, "E91", {"position": v(-50, -40.3) * mm});
            skPoint(sketch, "E92", {"position": v(-50, 40.3) * mm});
            skCircle(sketch, "E93", {"center": v(0, 120) * mm, "radius": 6 * mm});
            skLineSegment(sketch, "E94", {"start": v(0, 120) * mm, "end": v(0, 90) * mm, "construction": true});
            skArc(sketch, "E95", {"start": v(15, 120) * mm, "mid": v(0, 135) * mm, "end": v(-15, 120) * mm});
            skLineSegment(sketch, "E96", {"start": v(-15, 120) * mm, "end": v(-15, 108) * mm});
            skLineSegment(sketch, "E97", {"start": v(15, 120) * mm, "end": v(15, 108) * mm});
            skLineSegment(sketch, "E98", {"start": v(-15, 108) * mm, "end": v(-33, 90) * mm});
            skLineSegment(sketch, "E99", {"start": v(15, 108) * mm, "end": v(33, 90) * mm});
            skLineSegment(sketch, "E100", {"start": v(-80, 0) * mm, "end": v(80, 0) * mm, "construction": true});
            skCircle(sketch, "E101.MirrorC", {"center": v(0, -120) * mm, "radius": 6 * mm});
            skLineSegment(sketch, "E102.MirrorCS", {"start": v(0, -120) * mm, "end": v(0, -90) * mm, "construction": true});
            skArc(sketch, "E103.MirrorCS", {"start": v(15, -120) * mm, "mid": v(0, -135) * mm, "end": v(-15, -120) * mm});
            skLineSegment(sketch, "E104.MirrorCS", {"start": v(15, -108) * mm, "end": v(33, -90) * mm});
            skLineSegment(sketch, "E105.MirrorCS", {"start": v(-15, -120) * mm, "end": v(-15, -108) * mm});
            skLineSegment(sketch, "E106.MirrorCS", {"start": v(-15, -108) * mm, "end": v(-33, -90) * mm});
            skLineSegment(sketch, "E107.MirrorCS", {"start": v(15, -120) * mm, "end": v(15, -108) * mm});
            skSolve(sketch);
        }
        {
            var Q0;
            Q0=makeQuery(id+"F16.imprint","IMPRINT",FACE,{"disambiguationData":[TD([[makeQuery(id+"F16.imprint","IMPRINT",EDGE,{"derivedFrom":sQuery(id+"F16.wireOp",EDGE,"E93")}),-1.0]])]});
            var Q1;
            Q1=makeQuery(id+"F16.imprint","IMPRINT",FACE,{"disambiguationData":[TD([[makeQuery(id+"F16.imprint","IMPRINT",EDGE,{"derivedFrom":sQuery(id+"F16.wireOp",EDGE,"E101.MirrorC")}),1.0]])]});
            var Q2;
            Q2=makeQuery(id+"F16.imprint","IMPRINT",FACE,{"disambiguationData":[TD([[makeQuery(id+"F16.imprint","IMPRINT",EDGE,{"derivedFrom":makeQuery(id+"F1.opExtrude","CAP_EDGE",EDGE,{"disambiguationData":[OSD([sQuery(id+"F0.wireOp",EDGE,"E1.left")])],"isStart":true})}),-1.0]])]});
            var Q3;
            Q3=makeQuery(id+"F2.opExtrude","CAP_FACE",FACE,{"disambiguationData":[OSD([sQuery(id+"F0.wireOp",EDGE,"E12"),sQuery(id+"F0.wireOp",EDGE,"E13"),sQuery(id+"F0.wireOp",EDGE,"E14"),sQuery(id+"F0.wireOp",EDGE,"E15"),sQuery(id+"F0.wireOp",EDGE,"E17.filletArc"),sQuery(id+"F0.wireOp",EDGE,"E18.filletArc"),sQuery(id+"F0.wireOp",EDGE,"E19.filletArc"),sQuery(id+"F0.wireOp",EDGE,"E20.filletArc"),sQuery(id+"F0.wireOp",EDGE,"E25.0"),sQuery(id+"F0.wireOp",EDGE,"E25.1"),sQuery(id+"F0.wireOp",EDGE,"E25.2"),sQuery(id+"F0.wireOp",EDGE,"E25.3"),sQuery(id+"F0.wireOp",EDGE,"E25.4"),sQuery(id+"F0.wireOp",EDGE,"E25.5"),sQuery(id+"F0.wireOp",EDGE,"E25.6"),sQuery(id+"F0.wireOp",EDGE,"E25.7")])],"isStart":false});
            extrude(context, id + "F17", {"entities" : qUnion([Q0, Q1, Q2]), "endBound" : BoundingType.UP_TO_SURFACE, "endBoundEntityFace" : qUnion([Q3]), "depth" : 25 * mm});
        }
    });
